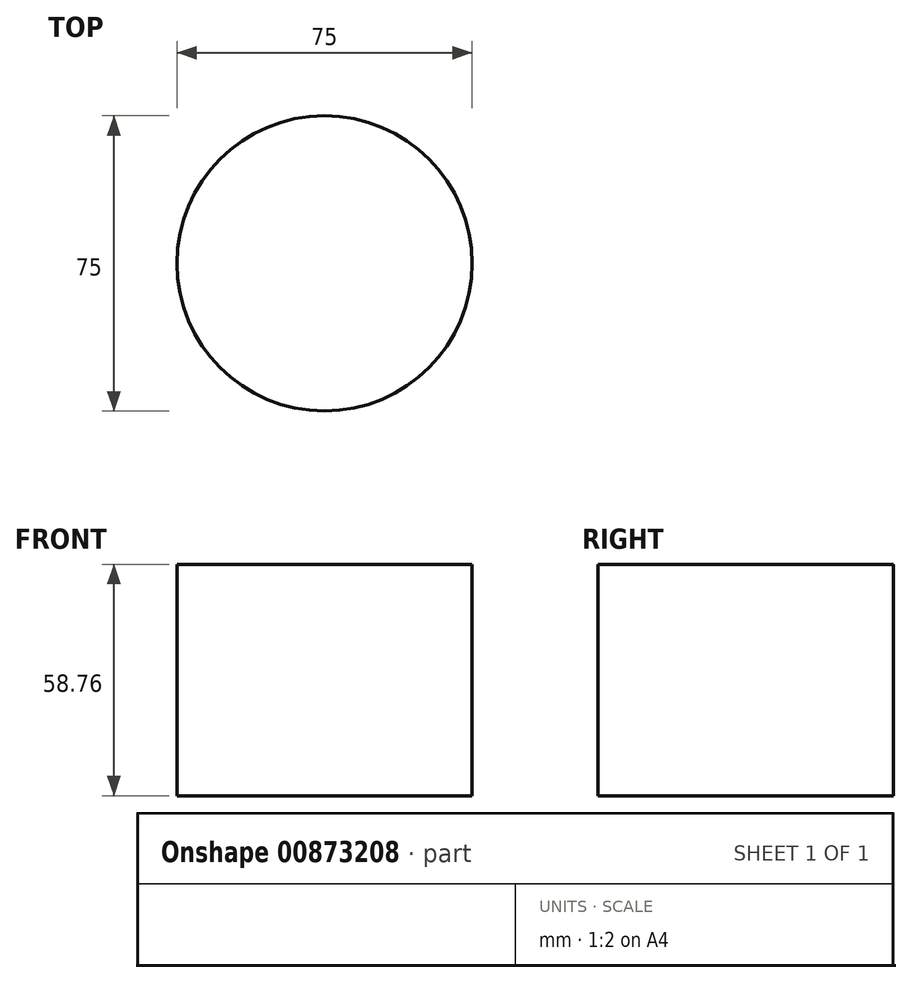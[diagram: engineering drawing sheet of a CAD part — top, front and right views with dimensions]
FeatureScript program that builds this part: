
annotation { "Feature Type Name" : "Feature", "Feature Type Description" : "" }
export const myFeature = defineFeature(function(context is Context, id is Id, definition is map)
    precondition{}
    {
        {
            var Q0;
            Q0=qCreatedBy(makeId("Top.planeOp"),FACE);
            var sketch = newSketch(context, id + "F0", { "sketchPlane" : qUnion([Q0])});
            skCircle(sketch, "E0", {"center": v(0, 0) * mm, "radius": 37.5 * mm});
            skSolve(sketch);
        }
        {
            var Q0;
            Q0=makeQuery(id+"F0.imprint","IMPRINT",FACE,{"disambiguationData":[TD([[makeQuery(id+"F0.imprint","IMPRINT",EDGE,{"derivedFrom":sQuery(id+"F0.wireOp",EDGE,"E0")}),1.0]])]});
            extrude(context, id + "F1", {"entities" : qUnion([Q0]), "depth" : 58.76 * mm, "offsetDistance" : 25 * mm});
        }
    });
